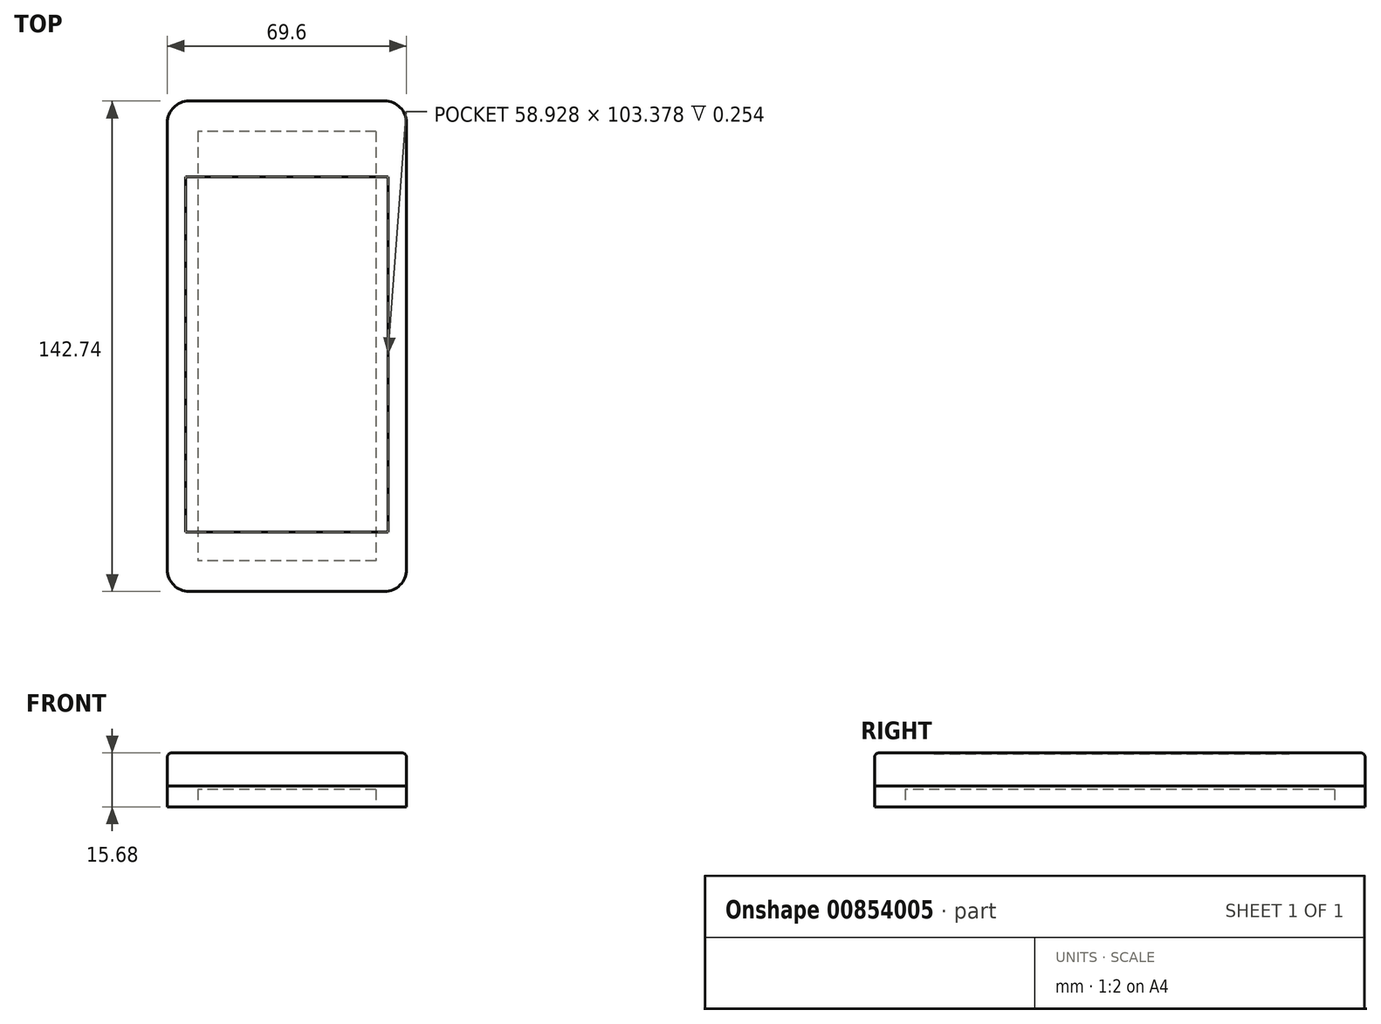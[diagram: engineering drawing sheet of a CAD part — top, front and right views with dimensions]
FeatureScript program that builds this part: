
annotation { "Feature Type Name" : "Feature", "Feature Type Description" : "" }
export const myFeature = defineFeature(function(context is Context, id is Id, definition is map)
    precondition{}
    {
        {
            var Q0;
            Q0=qCreatedBy(makeId("Top.planeOp"),FACE);
            var sketch = newSketch(context, id + "F0", { "sketchPlane" : qUnion([Q0])});
            skLineSegment(sketch, "E0.bottom", {"start": v(28.45, 71.37) * mm, "end": v(-28.45, 71.37) * mm});
            skLineSegment(sketch, "E0.top", {"start": v(28.45, -71.37) * mm, "end": v(-28.45, -71.37) * mm});
            skLineSegment(sketch, "E0.left", {"start": v(34.8, 65.02) * mm, "end": v(34.8, -65.02) * mm});
            skLineSegment(sketch, "E0.right", {"start": v(-34.8, 65.02) * mm, "end": v(-34.8, -65.02) * mm});
            skPoint(sketch, "E0.middle", {"position": v(0, 0) * mm});
            skPoint(sketch, "E1.visualSharp", {"position": v(-34.8, 71.37) * mm});
            skArc(sketch, "E1.filletArc", {"start": v(-28.45, 71.37) * mm, "mid": v(-32.94, 69.51) * mm, "end": v(-34.8, 65.02) * mm});
            skPoint(sketch, "E2.visualSharp", {"position": v(34.8, 71.37) * mm});
            skArc(sketch, "E2.filletArc", {"start": v(34.8, 65.02) * mm, "mid": v(32.94, 69.51) * mm, "end": v(28.45, 71.37) * mm});
            skPoint(sketch, "E3.visualSharp", {"position": v(34.8, -71.37) * mm});
            skArc(sketch, "E3.filletArc", {"start": v(28.45, -71.37) * mm, "mid": v(32.94, -69.51) * mm, "end": v(34.8, -65.02) * mm});
            skPoint(sketch, "E4.visualSharp", {"position": v(-34.8, -71.37) * mm});
            skArc(sketch, "E4.filletArc", {"start": v(-34.8, -65.02) * mm, "mid": v(-32.94, -69.51) * mm, "end": v(-28.45, -71.37) * mm});
            skSolve(sketch);
        }
        {
            var Q0;
            Q0=makeQuery(id+"F0.imprint","IMPRINT",FACE,{"disambiguationData":[TD([[makeQuery(id+"F0.imprint","IMPRINT",EDGE,{"derivedFrom":sQuery(id+"F0.wireOp",EDGE,"E0.bottom")}),1.0]])]});
            extrude(context, id + "F1", {"entities" : qUnion([Q0]), "depth" : 9.68 * mm, "offsetDistance" : 25.4 * mm});
        }
        {
            var Q0;
            Q0=makeQuery(id+"F1.opExtrude","CAP_FACE",FACE,{"disambiguationData":[OSD([sQuery(id+"F0.wireOp",EDGE,"E0.bottom"),sQuery(id+"F0.wireOp",EDGE,"E0.top"),sQuery(id+"F0.wireOp",EDGE,"E0.left"),sQuery(id+"F0.wireOp",EDGE,"E0.right"),sQuery(id+"F0.wireOp",EDGE,"E1.filletArc"),sQuery(id+"F0.wireOp",EDGE,"E2.filletArc"),sQuery(id+"F0.wireOp",EDGE,"E3.filletArc"),sQuery(id+"F0.wireOp",EDGE,"E4.filletArc")])],"isStart":false});
            var sketch = newSketch(context, id + "F2", { "sketchPlane" : qUnion([Q0])});
            skLineSegment(sketch, "E5.bottom", {"start": v(29.46, -54.1) * mm, "end": v(-29.46, -54.1) * mm});
            skLineSegment(sketch, "E5.top", {"start": v(29.46, 49.28) * mm, "end": v(-29.46, 49.28) * mm});
            skLineSegment(sketch, "E5.left", {"start": v(29.46, -54.1) * mm, "end": v(29.46, 49.28) * mm});
            skLineSegment(sketch, "E5.right", {"start": v(-29.46, -54.1) * mm, "end": v(-29.46, 49.28) * mm});
            skPoint(sketch, "E5.middle", {"position": v(0, -2.41) * mm});
            skSolve(sketch);
        }
        {
            var Q0;
            Q0 = qSketchRegion(id + "F2", true);
            extrude(context, id + "F3", {"entities" : qUnion([Q0]), "operationType" : NewBodyOperationType.REMOVE, "oppositeDirection" : true, "depth" : 0.25 * mm, "offsetDistance" : 25.4 * mm});
        }
        {
            var Q0;
            Q0=makeQuery(id+"F1.opExtrude","CAP_FACE",FACE,{"disambiguationData":[OSD([sQuery(id+"F0.wireOp",EDGE,"E0.bottom"),sQuery(id+"F0.wireOp",EDGE,"E0.top"),sQuery(id+"F0.wireOp",EDGE,"E0.left"),sQuery(id+"F0.wireOp",EDGE,"E0.right"),sQuery(id+"F0.wireOp",EDGE,"E1.filletArc"),sQuery(id+"F0.wireOp",EDGE,"E2.filletArc"),sQuery(id+"F0.wireOp",EDGE,"E3.filletArc"),sQuery(id+"F0.wireOp",EDGE,"E4.filletArc")])],"isStart":true});
            var sketch = newSketch(context, id + "F4", { "sketchPlane" : qUnion([Q0])});
            skLineSegment(sketch, "E6.0.0", {"start": v(28.45, 71.37) * mm, "end": v(-28.45, 71.37) * mm});
            skArc(sketch, "E6.0.1", {"start": v(-28.45, 71.37) * mm, "mid": v(-32.94, 69.51) * mm, "end": v(-34.8, 65.02) * mm});
            skLineSegment(sketch, "E6.0.2", {"start": v(-34.8, 65.02) * mm, "end": v(-34.8, -65.02) * mm});
            skArc(sketch, "E6.0.3", {"start": v(-34.8, -65.02) * mm, "mid": v(-32.94, -69.51) * mm, "end": v(-28.45, -71.37) * mm});
            skLineSegment(sketch, "E6.0.4", {"start": v(-28.45, -71.37) * mm, "end": v(28.45, -71.37) * mm});
            skArc(sketch, "E6.0.5", {"start": v(28.45, -71.37) * mm, "mid": v(32.94, -69.51) * mm, "end": v(34.8, -65.02) * mm});
            skLineSegment(sketch, "E6.0.6", {"start": v(34.8, -65.02) * mm, "end": v(34.8, 65.02) * mm});
            skArc(sketch, "E6.0.7", {"start": v(34.8, 65.02) * mm, "mid": v(32.94, 69.51) * mm, "end": v(28.45, 71.37) * mm});
            skSolve(sketch);
        }
        {
            var Q0;
            Q0 = qSketchRegion(id + "F4", true);
            extrude(context, id + "F5", {"entities" : qUnion([Q0]), "depth" : 6 * mm, "offsetDistance" : 25.4 * mm});
        }
        {
            var Q0;
            Q0=makeQuery(id+"F1.opExtrude","CAP_EDGE",EDGE,{"disambiguationData":[OSD([sQuery(id+"F0.wireOp",EDGE,"E0.right")])],"isStart":false});
            fillet(context, id + "F6", {"entities" : qUnion([Q0]), "radius" : 1.27 * mm, "tangentPropagation" : true, "allowEdgeOverflow" : false});
        }
        {
            var Q0;
            Q0=makeQuery(id+"F5.opExtrude","CAP_FACE",FACE,{"disambiguationData":[OSD([sQuery(id+"F4.wireOp",EDGE,"E6.0.0"),sQuery(id+"F4.wireOp",EDGE,"E6.0.1"),sQuery(id+"F4.wireOp",EDGE,"E6.0.2"),sQuery(id+"F4.wireOp",EDGE,"E6.0.3"),sQuery(id+"F4.wireOp",EDGE,"E6.0.4"),sQuery(id+"F4.wireOp",EDGE,"E6.0.5"),sQuery(id+"F4.wireOp",EDGE,"E6.0.6"),sQuery(id+"F4.wireOp",EDGE,"E6.0.7")])],"isStart":false});
            var sketch = newSketch(context, id + "F7", { "sketchPlane" : qUnion([Q0])});
            skLineSegment(sketch, "E7.0", {"start": v(28.45, -71.37) * mm, "end": v(-28.45, -71.37) * mm});
            skPoint(sketch, "E8.0", {"position": v(32.94, -69.51) * mm});
            skArc(sketch, "E9.0", {"start": v(34.8, -65.02) * mm, "mid": v(32.94, -69.51) * mm, "end": v(28.45, -71.37) * mm});
            skLineSegment(sketch, "E10.0", {"start": v(34.8, -65.02) * mm, "end": v(34.8, 65.02) * mm});
            skArc(sketch, "E11.0", {"start": v(28.45, 71.37) * mm, "mid": v(32.94, 69.51) * mm, "end": v(34.8, 65.02) * mm});
            skLineSegment(sketch, "E12.0", {"start": v(28.45, 71.37) * mm, "end": v(-28.45, 71.37) * mm});
            skArc(sketch, "E13.0", {"start": v(-34.8, 65.02) * mm, "mid": v(-32.94, 69.51) * mm, "end": v(-28.45, 71.37) * mm});
            skLineSegment(sketch, "E14.0", {"start": v(-34.8, -65.02) * mm, "end": v(-34.8, 65.02) * mm});
            skArc(sketch, "E15.0", {"start": v(-28.45, -71.37) * mm, "mid": v(-32.94, -69.51) * mm, "end": v(-34.8, -65.02) * mm});
            skLineSegment(sketch, "E16.0", {"start": v(25.9, -62.48) * mm, "end": v(-25.9, -62.48) * mm});
            skLineSegment(sketch, "E16.1", {"start": v(25.9, -62.48) * mm, "end": v(25.9, 62.48) * mm});
            skLineSegment(sketch, "E16.2", {"start": v(25.9, 62.48) * mm, "end": v(-25.9, 62.48) * mm});
            skLineSegment(sketch, "E16.3", {"start": v(-25.9, -62.48) * mm, "end": v(-25.9, 62.48) * mm});
            skSolve(sketch);
        }
        {
            var Q0;
            Q0=makeQuery(id+"F7.imprint","IMPRINT",FACE,{"disambiguationData":[TD([[makeQuery(id+"F7.imprint","IMPRINT",EDGE,{"derivedFrom":sQuery(id+"F7.wireOp",EDGE,"E16.0")}),-1.0]])]});
            extrude(context, id + "F8", {"entities" : qUnion([Q0]), "operationType" : NewBodyOperationType.REMOVE, "oppositeDirection" : true, "depth" : 5 * mm, "offsetDistance" : 25.4 * mm});
        }
    });
